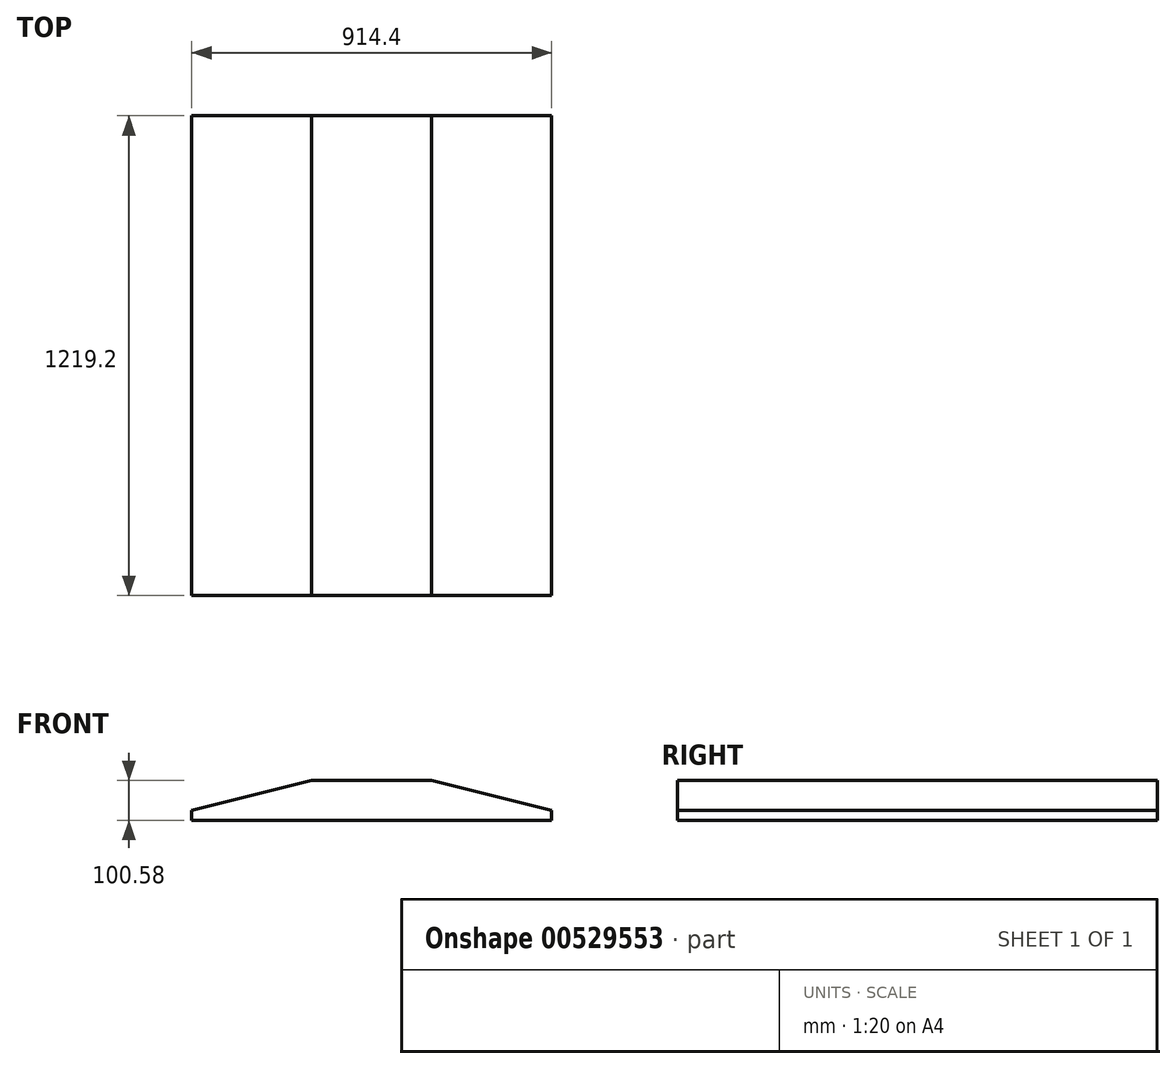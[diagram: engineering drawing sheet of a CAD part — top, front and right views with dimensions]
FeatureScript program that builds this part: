
annotation { "Feature Type Name" : "Feature", "Feature Type Description" : "" }
export const myFeature = defineFeature(function(context is Context, id is Id, definition is map)
    precondition{}
    {
        {
            var Q0;
            Q0=qCreatedBy(makeId("Top.planeOp"),FACE);
            var sketch = newSketch(context, id + "F0", { "sketchPlane" : qUnion([Q0])});
            skLineSegment(sketch, "E0.bottom", {"start": v(-3421.22, 0) * mm, "end": v(-2506.82, 0) * mm});
            skLineSegment(sketch, "E0.top", {"start": v(-3421.22, 1219.2) * mm, "end": v(-2506.82, 1219.2) * mm});
            skLineSegment(sketch, "E0.left", {"start": v(-3421.22, 0) * mm, "end": v(-3421.22, 1219.2) * mm});
            skLineSegment(sketch, "E0.right", {"start": v(-2506.82, 0) * mm, "end": v(-2506.82, 1219.2) * mm});
            skSolve(sketch);
        }
        {
            var Q0;
            Q0=makeQuery(id+"F0.imprint","IMPRINT",FACE,{"disambiguationData":[TD([[makeQuery(id+"F0.imprint","IMPRINT",EDGE,{"derivedFrom":sQuery(id+"F0.wireOp",EDGE,"E0.bottom")}),1.0]])]});
            var Q1;
            Q1=sQuery(id+"F0.wireOp",EDGE,"E0.left");
            extrude(context, id + "F1", {"entities" : qUnion([Q0]), "surfaceEntities" : qUnion([Q1]), "depth" : 100.58 * mm, "offsetDistance" : 30.48 * mm});
        }
        {
            var Q0;
            Q0=makeQuery(id+"F1.opExtrude","CAP_EDGE",EDGE,{"disambiguationData":[OSD([sQuery(id+"F0.wireOp",EDGE,"E0.left")])],"isStart":false});
            chamfer(context, id + "F2", {"entities" : qUnion([Q0]), "chamferType" : ChamferType.TWO_OFFSETS, "width1" : 76.2 * mm, "oppositeDirection" : false, "width2" : 304.8 * mm, "tangentPropagation" : true});
        }
        {
            var Q0;
            Q0=makeQuery(id+"F1.opExtrude","CAP_EDGE",EDGE,{"disambiguationData":[OSD([sQuery(id+"F0.wireOp",EDGE,"E0.right")])],"isStart":false});
            chamfer(context, id + "F3", {"entities" : qUnion([Q0]), "chamferType" : ChamferType.TWO_OFFSETS, "width1" : 304.8 * mm, "oppositeDirection" : false, "width2" : 76.2 * mm, "tangentPropagation" : true});
        }
    });
